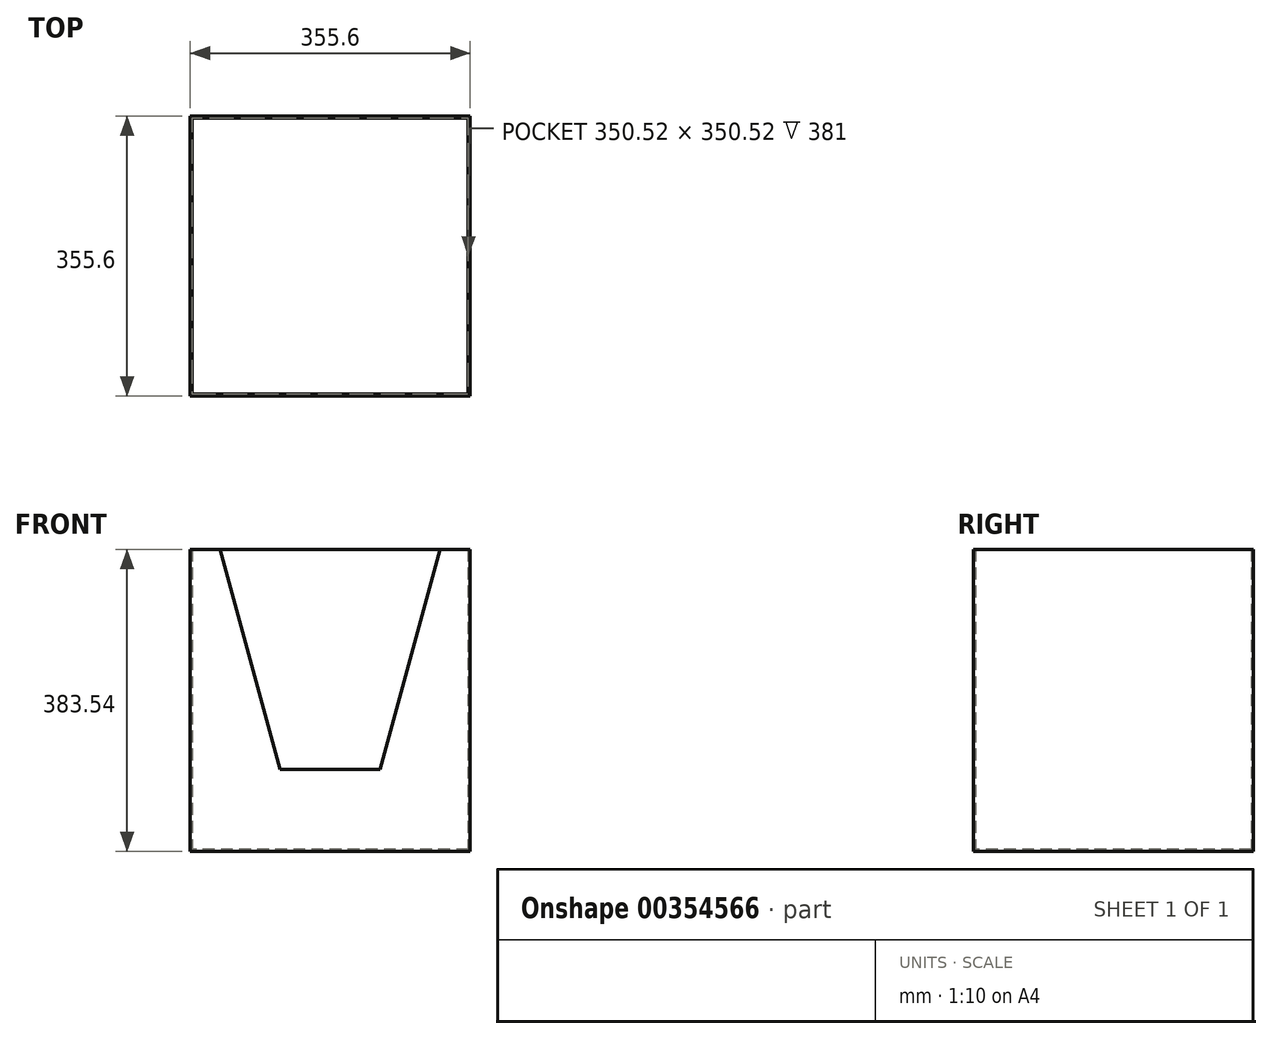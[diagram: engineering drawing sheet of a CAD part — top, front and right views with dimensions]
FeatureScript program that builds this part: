
annotation { "Feature Type Name" : "Feature", "Feature Type Description" : "" }
export const myFeature = defineFeature(function(context is Context, id is Id, definition is map)
    precondition{}
    {
        {
            var Q0;
            Q0=qCreatedBy(makeId("Top.planeOp"),FACE);
            var sketch = newSketch(context, id + "F0", { "sketchPlane" : qUnion([Q0])});
            skLineSegment(sketch, "E0.bottom", {"start": v(177.8, 177.8) * mm, "end": v(-177.8, 177.8) * mm});
            skLineSegment(sketch, "E0.top", {"start": v(177.8, -177.8) * mm, "end": v(-177.8, -177.8) * mm});
            skLineSegment(sketch, "E0.left", {"start": v(177.8, 177.8) * mm, "end": v(177.8, -177.8) * mm});
            skLineSegment(sketch, "E0.right", {"start": v(-177.8, 177.8) * mm, "end": v(-177.8, -177.8) * mm});
            skPoint(sketch, "E0.middle", {"position": v(0, 0) * mm});
            skSolve(sketch);
        }
        {
            var Q0;
            Q0=makeQuery(id+"F0.imprint","IMPRINT",FACE,{"disambiguationData":[TD([[makeQuery(id+"F0.imprint","IMPRINT",EDGE,{"derivedFrom":sQuery(id+"F0.wireOp",EDGE,"E0.bottom")}),1.0]])]});
            extrude(context, id + "F1", {"entities" : qUnion([Q0]), "depth" : 383.54 * mm});
        }
        {
            var Q0;
            Q0=makeQuery(id+"F1.opExtrude","CAP_FACE",FACE,{"disambiguationData":[OSD([sQuery(id+"F0.wireOp",EDGE,"E0.bottom"),sQuery(id+"F0.wireOp",EDGE,"E0.top"),sQuery(id+"F0.wireOp",EDGE,"E0.left"),sQuery(id+"F0.wireOp",EDGE,"E0.right")])],"isStart":false});
            shell(context, id + "F2", {"entities" : qUnion([Q0]), "thickness" : 2.54 * mm});
        }
        {
            var Q0;
            Q0=makeQuery(id+"F1.opExtrude","SWEPT_FACE",FACE,{"disambiguationData":[OSD([sQuery(id+"F0.wireOp",EDGE,"E0.top")])]});
            var sketch = newSketch(context, id + "F3", { "sketchPlane" : qUnion([Q0])});
            skLineSegment(sketch, "E1", {"start": v(-139.7, 383.54) * mm, "end": v(-63.5, 104.14) * mm});
            skLineSegment(sketch, "E2", {"start": v(-63.5, 104.14) * mm, "end": v(63.5, 104.14) * mm});
            skLineSegment(sketch, "E3", {"start": v(63.5, 104.14) * mm, "end": v(139.7, 383.54) * mm});
            skLineSegment(sketch, "E4", {"start": v(139.7, 383.54) * mm, "end": v(-139.7, 383.54) * mm});
            skPoint(sketch, "E5", {"position": v(0, 104.14) * mm});
            skPoint(sketch, "E6", {"position": v(0, 383.54) * mm});
            skSolve(sketch);
        }
        {
            var Q0;
            Q0=makeQuery(id+"F3.imprint","IMPRINT",FACE,{"disambiguationData":[TD([[makeQuery(id+"F3.imprint","IMPRINT",EDGE,{"derivedFrom":sQuery(id+"F3.wireOp",EDGE,"E1")}),1.0]])]});
            extrude(context, id + "F4", {"entities" : qUnion([Q0]), "operationType" : NewBodyOperationType.REMOVE, "oppositeDirection" : true, "depth" : 25.4 * mm});
        }
    });
